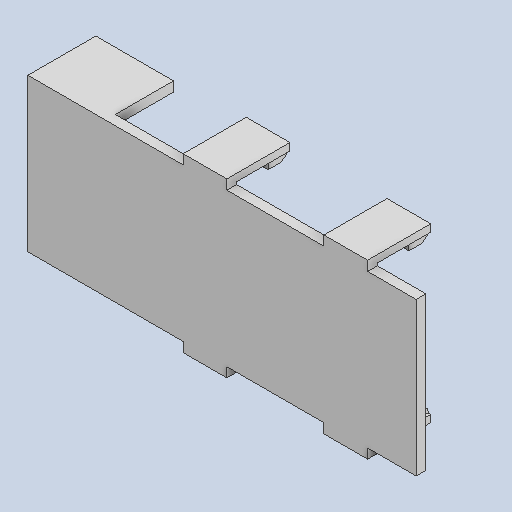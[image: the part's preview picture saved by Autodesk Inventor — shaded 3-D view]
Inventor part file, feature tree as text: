
AUTODESK INVENTOR PART (.ipt)
format: ipt  version: 2025 (Build 290162000, 162)  size: 331,776 bytes
history: native  units: mm
features: reference x21, extrude x6, other x3, plane x1, chamfer x1, sketch x1
ambient origin geometry x8: Origin, YZ Plane, XZ Plane, XY Plane, X Axis, Y Axis, Z Axis, Center Point
bodies: Solid1 (feature_tree)
feature tree (33):
  extrude  "Extrusion1"  Depth=0.4mm
  plane  "Work Plane1"
  extrude  "Extrusion2"  Depth=0.1mm
  extrude  "Extrusion3"  Depth=0.1mm
  extrude  "Extrusion4"  Depth=0.4mm TaperAngle=0.0deg
  chamfer  "Chamfer1"  Distance=0.1mm
  extrude  "Extrusion5"  Depth=0.2mm
  extrude  "Extrusion6"  Depth=0.1mm
  sketch  "Sketch1"  dims[d0=0.4mm d1=0.0mm d2=0.4mm d3=0.1mm d4=0.1mm d5=0.4mm d6=0.0mm d7=0.1mm d8=0.2mm d9=0.1mm d10=0.1mm d11=0.2mm d12=0.1mm d13=0.35mm d14=-0.872665mm d15=0.35mm d16=-0.872665mm d17=0.2mm d18=2.0mm d19=45.0deg d20=0.2mm d21=0.2mm d22=2.4mm d23=0.0mm d24=0.3mm d25=2.1mm d26=0.0mm]
  reference  "Reference1"
  reference  "Reference5"
  reference  "Reference6"
  reference  "Reference7"
  reference  "Reference8"
  reference  "Reference9"
  reference  "Reference10"
  reference  "Reference11"
  reference  "Reference12"
  reference  "Reference13"
  reference  "Reference14"
  reference  "Reference15"
  reference  "Reference16"
  reference  "Reference17"
  reference  "Reference18"
  reference  "Reference19"
  reference  "Reference20"
  reference  "Reference21"
  reference  "Reference22"
  reference  "Reference23"
  reference  "Reference24"
  parser-record x1  (decoder bookkeeping rows leaked as tree rows — omitted from the tree; the rows remain in map.json)
  other  "np2_full_assembly.iam"
  other  "np2_main_chassis:1"
note: 1 file-system path scrubbed to <path> (originals preserved in map.json)
